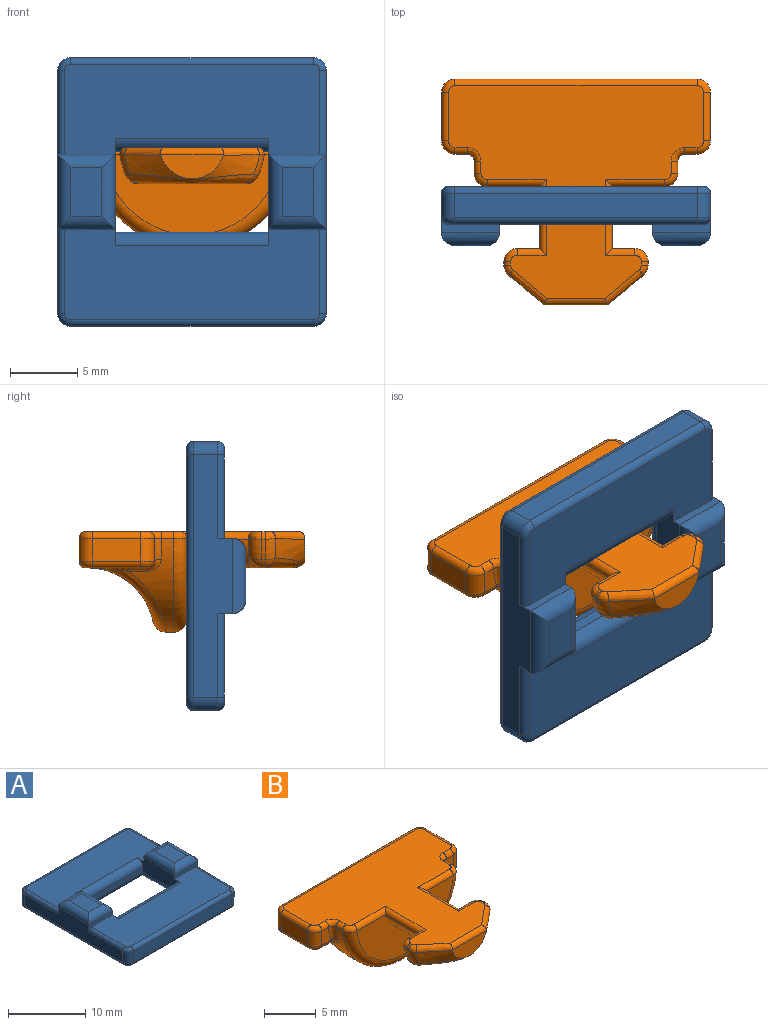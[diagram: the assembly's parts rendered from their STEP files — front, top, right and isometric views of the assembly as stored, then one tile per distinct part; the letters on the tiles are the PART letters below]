
ASSEMBLY  parts=2 mates=1
PART A: 53 faces, bbox 20.2x20.2x4.4 mm
  f0: plane 19x6.7mm, normal (0,0,1), area 113.5mm2, adj f6,f8,f12,f15,f33,f48,f49,f50
  f1: plane 19x6.7mm, normal (0,0,1), area 113.5mm2, adj f6,f8,f11,f14,f34,f43,f44,f45
  f2: plane 18x2.9mm, normal (1,0,0), area 38.6mm2, adj f11,f12,f18,f26,f28,f38,f47,f52
  f3: plane 18x1.8mm, normal (0,1,0), area 32.4mm2, adj f27,f28,f35,f45
  f4: plane 18x2.9mm, normal (-1,0,0), area 38.6mm2, adj f14,f15,f22,f25,f27,f39,f43,f48
  f5: plane 11.4x0.8mm, normal (0,-1,0), area 9.1mm2, adj f6,f8,f30,f34
  f6: plane 8x2.4mm, normal (-1,0,0), area 14.6mm2, adj f0,f1,f5,f7,f11,f12,f19,f29
  f7: plane 11.4x0.8mm, normal (0,1,0), area 9.1mm2, adj f6,f8,f31,f33
  f8: plane 8x2.4mm, normal (1,0,0), area 14.6mm2, adj f0,f1,f5,f7,f14,f15,f23,f32
  f9: plane 18x1.8mm, normal (0,-1,0), area 32.4mm2, adj f25,f26,f42,f50
  f10: plane 19x19mm, normal (0,0,-1), area 253.6mm2, adj f29,f30,f31,f32,f35,f36,f37,f38
  f11: plane 4.3x1.1mm, normal (0,1,0), area 2.6mm2, adj f1,f2,f6,f17,f47
  f12: plane 4.3x1.1mm, normal (0,-1,0), area 2.6mm2, adj f0,f2,f6,f20,f52
  f13: plane 3.6x2.3mm, normal (0,0,1), area 8.3mm2, adj f17,f18,f19,f20
  f14: plane 4.3x1.1mm, normal (0,1,0), area 2.6mm2, adj f1,f4,f8,f24,f43
  f15: plane 4.3x1.1mm, normal (0,-1,0), area 2.6mm2, adj f0,f4,f8,f21,f48
  f16: plane 3.6x2.3mm, normal (0,0,1), area 8.3mm2, adj f21,f22,f23,f24
  f17: cylinder r=1mm len=4.3mm, axis (1,0,0), area 5.6mm2, adj f11,f13,f18,f19
  f18: cylinder r=1mm len=5.6mm, axis (0,-1,0), area 7.7mm2, adj f2,f13,f17,f20
  f19: cylinder r=1mm len=5.6mm, axis (0,1,0), area 7.7mm2, adj f6,f13,f17,f20
  f20: cylinder r=1mm len=4.3mm, axis (-1,0,0), area 5.6mm2, adj f12,f13,f18,f19
  f21: cylinder r=1mm len=4.3mm, axis (-1,0,0), area 5.6mm2, adj f15,f16,f22,f23
  f22: cylinder r=1mm len=5.6mm, axis (0,1,0), area 7.7mm2, adj f4,f16,f21,f24
  f23: cylinder r=1mm len=5.6mm, axis (0,-1,0), area 7.7mm2, adj f8,f16,f21,f24
  f24: cylinder r=1mm len=4.3mm, axis (1,0,0), area 5.6mm2, adj f14,f16,f22,f23
  f25: cylinder r=1mm len=1.8mm, axis (0,0,1), area 2.8mm2, adj f4,f9,f41,f49
  f26: cylinder r=1mm len=1.8mm, axis (0,0,-1), area 2.8mm2, adj f2,f9,f40,f51
  f27: cylinder r=1mm len=1.8mm, axis (0,0,-1), area 2.8mm2, adj f3,f4,f37,f44
  f28: cylinder r=1mm len=1.8mm, axis (0,0,1), area 2.8mm2, adj f2,f3,f36,f46
  f29: cylinder r=1mm len=8mm, axis (0,-1,0), area 10.6mm2, adj f6,f10,f30,f31
  f30: cylinder r=1mm len=13.4mm, axis (1,0,0), area 19mm2, adj f5,f10,f29,f32
  f31: cylinder r=1mm len=13.4mm, axis (-1,0,0), area 19mm2, adj f7,f10,f29,f32
  f32: cylinder r=1mm len=8mm, axis (0,1,0), area 10.6mm2, adj f8,f10,f30,f31
  f33: cylinder r=1mm len=11.4mm, axis (1,0,0), area 17.9mm2, adj f0,f6,f7,f8
  f34: cylinder r=1mm len=11.4mm, axis (-1,0,0), area 17.9mm2, adj f1,f5,f6,f8
  f35: cylinder r=0.5mm len=18mm, axis (-1,0,0), area 14.1mm2, adj f3,f10,f36,f37
  f36: torus R=0.5mm, axis (0,0,1), area 1mm2, adj f10,f28,f35,f38
  f37: torus R=0.5mm, axis (0,0,1), area 1mm2, adj f10,f27,f35,f39
  f38: cylinder r=0.5mm len=18mm, axis (0,1,0), area 14.1mm2, adj f2,f10,f36,f40
  f39: cylinder r=0.5mm len=18mm, axis (0,-1,0), area 14.1mm2, adj f4,f10,f37,f41
  f40: torus R=0.5mm, axis (0,0,1), area 1mm2, adj f10,f26,f38,f42
  f41: torus R=0.5mm, axis (0,0,1), area 1mm2, adj f10,f25,f39,f42
  f42: cylinder r=0.5mm len=18mm, axis (1,0,0), area 14.1mm2, adj f9,f10,f40,f41
  f43: cylinder r=0.5mm len=6.2mm, axis (0,1,0), area 4.9mm2, adj f1,f4,f14,f44
  f44: torus R=0.5mm, axis (0,0,1), area 1mm2, adj f1,f27,f43,f45
  f45: cylinder r=0.5mm len=18mm, axis (1,0,0), area 14.1mm2, adj f1,f3,f44,f46
  f46: torus R=0.5mm, axis (0,0,1), area 1mm2, adj f1,f28,f45,f47
  f47: cylinder r=0.5mm len=6.2mm, axis (0,-1,0), area 4.9mm2, adj f1,f2,f11,f46
  f48: cylinder r=0.5mm len=6.2mm, axis (0,1,0), area 4.9mm2, adj f0,f4,f15,f49
  f49: torus R=0.5mm, axis (0,0,1), area 1mm2, adj f0,f25,f48,f50
  f50: cylinder r=0.5mm len=18mm, axis (-1,0,0), area 14.1mm2, adj f0,f9,f49,f51
  f51: torus R=0.5mm, axis (0,0,1), area 1mm2, adj f0,f26,f50,f52
  f52: cylinder r=0.5mm len=6.2mm, axis (0,-1,0), area 4.9mm2, adj f0,f2,f12,f51
PART B: 86 faces, bbox 40.2x41.7x32.7 mm
  f0: plane 3.6x1.7mm, normal (-1,0,0), area 6.1mm2, adj f1,f83,f84,f85
  f1: cylinder r=0.5mm len=3.6mm, axis (0,1,0), area 2.8mm2, adj f0,f2,f81,f82
  f2: plane 39x24.6mm, normal (0,0,-1), area 22.9mm2, adj f1,f3,f71,f72,f73,f74,f75,f76
  f3: cylinder r=0.5mm len=1.6mm, axis (1,0,0), area 1.1mm2, adj f2,f4,f70,f71
  f4: bspline ~1.21x1.06mm, area 0.8mm2, adj f3,f5,f68,f80
  f5: torus R=8.1mm, axis (0,-1,0), area 1.3mm2, adj f4,f6,f68,f70
  f6: bspline ~1.23x1.06mm, area 0.9mm2, adj f5,f7,f66,f67
  f7: plane 19x15.8mm, normal (0,0,1), area 171.3mm2, adj f6,f8,f12,f13,f14,f15,f20,f21
  f8: bspline ~1.23x1.22mm, area 0.9mm2, adj f7,f9,f12,f65
  f9: torus R=8.1mm, axis (0,-1,0), area 1.3mm2, adj f8,f10,f11,f68
  f10: plane 1.72x1.23mm, normal (0,-1,0), area 1.8mm2, adj f9,f12,f75,f85
  f11: bspline ~1.15x1.06mm, area 0.8mm2, adj f9,f68,f75,f76
  f12: cylinder r=0.5mm len=0.92mm, axis (-1,0,0), area 0.7mm2, adj f7,f8,f10,f13
  f13: torus R=0.5mm, axis (0,0,1), area 1mm2, adj f7,f12,f84,f85
  f14: torus R=0.5mm, axis (0,0,1), area 1mm2, adj f7,f15,f83,f84
  f15: cylinder r=0.5mm len=18mm, axis (1,0,0), area 14.1mm2, adj f7,f14,f16,f20
  f16: plane 18x1.7mm, normal (0,1,0), area 30.6mm2, adj f15,f17,f74,f83
  f17: cylinder r=1mm len=1.7mm, axis (0,0,1), area 2.7mm2, adj f16,f18,f20,f73
  f18: plane 3.6x1.7mm, normal (1,0,0), area 6.1mm2, adj f17,f19,f21,f72
  f19: cylinder r=1mm len=1.7mm, axis (0,0,-1), area 2.7mm2, adj f18,f22,f70,f71
  f20: torus R=0.5mm, axis (0,0,1), area 1mm2, adj f7,f15,f17,f21
  f21: cylinder r=0.5mm len=3.6mm, axis (0,-1,0), area 2.8mm2, adj f7,f18,f20,f22
  f22: torus R=0.5mm, axis (0,0,1), area 1mm2, adj f7,f19,f21,f66
  f23: bspline ~1.23x1.1mm, area 1.1mm2, adj f7,f24,f49,f67
  f24: torus R=6.6mm, axis (0,1,0), area 33.7mm2, adj f23,f25,f64,f68
  f25: plane 13.2x6.05mm, normal (0,-1,0), area 51.5mm2, adj f24,f26,f49,f50,f62,f63
  f26: cylinder r=2.8mm len=5.41mm, axis (0,1,0), area 33.7mm2, adj f25,f27,f46,f47,f48,f50,f62
  f27: plane 2.24x1.22mm, normal (0,1,0), area 2.1mm2, adj f26,f28,f45,f61,f62
  f28: cylinder r=1mm len=1.87mm, axis (1,0,0), area 2.9mm2, adj f27,f29,f44,f46
  f29: sphere r=1mm, area 1.2mm2, adj f28,f30,f45
  f30: cylinder r=1mm len=0.91mm, axis (0,1,0), area 0.3mm2, adj f29,f31,f43,f44
  f31: cylinder r=5.4mm len=1.55mm, axis (0,1,0), area 0.4mm2, adj f30,f32,f45,f59
  f32: torus R=4.4mm, axis (0,1,0), area 1.4mm2, adj f31,f33,f43,f58
  f33: cone r=5.4mm half-angle=50deg, axis (0,1,0), area 11.6mm2, adj f32,f34,f41,f42,f55,f57
  f34: bspline ~10.74x3.6mm, area 10.9mm2, adj f33,f35,f43,f44
  f35: sphere r=1mm, area 0.6mm2, adj f34,f36,f42
  f36: cylinder r=1mm len=0.91mm, axis (0,1,0), area 0.3mm2, adj f35,f37,f39,f44
  f37: cylinder r=5.4mm len=1.55mm, axis (0,1,0), area 0.4mm2, adj f36,f38,f42,f53
  f38: torus R=4.4mm, axis (0,-1,0), area 2.3mm2, adj f37,f39,f48,f52
  f39: sphere r=1mm, area 1.2mm2, adj f36,f38,f40
  f40: cylinder r=1mm len=1.87mm, axis (1,0,0), area 2.9mm2, adj f39,f44,f47,f48
  f41: plane 4.67x1.83mm, normal (0,-1,0), area 6.3mm2, adj f33,f55,f56,f57
  f42: torus R=4.4mm, axis (0,-1,0), area 1.4mm2, adj f33,f35,f37,f54
  f43: sphere r=1mm, area 0.6mm2, adj f30,f32,f34
  f44: plane 8.03x3.42mm, normal (0,0,-1), area 14.1mm2, adj f28,f30,f34,f36,f40,f46,f47
  f45: torus R=4.4mm, axis (0,-1,0), area 2.3mm2, adj f27,f29,f31,f60
  f46: bspline ~2.44x1.15mm, area 1.1mm2, adj f26,f28,f44
  f47: bspline ~2.44x1.15mm, area 1.1mm2, adj f26,f40,f44
  f48: plane 2.24x1.22mm, normal (0,1,0), area 2.1mm2, adj f26,f38,f40,f50,f51
  f49: cylinder r=0.5mm len=4.35mm, axis (-1,0,0), area 3.2mm2, adj f7,f23,f25,f50
  f50: cylinder r=0.5mm len=5.6mm, axis (0,1,0), area 4.5mm2, adj f7,f25,f26,f48,f49,f51
  f51: cylinder r=0.5mm len=2.14mm, axis (1,0,0), area 1.5mm2, adj f7,f48,f50,f52
  f52: bspline ~1.24x1.13mm, area 1.1mm2, adj f7,f38,f51,f53
  f53: cylinder r=0.5mm len=0.56mm, axis (0,1,0), area 0.2mm2, adj f7,f37,f52,f54
  f54: bspline ~1.07x0.77mm, area 0.6mm2, adj f7,f42,f53,f55
  f55: bspline ~4.22x3.68mm, area 2.9mm2, adj f7,f33,f41,f54,f56
  f56: cylinder r=0.5mm len=4.67mm, axis (-1,0,0), area 3.5mm2, adj f7,f41,f55,f57
  f57: bspline ~4.22x3.68mm, area 2.9mm2, adj f7,f33,f41,f56,f58
  f58: bspline ~0.98x0.84mm, area 0.6mm2, adj f7,f32,f57,f59
  f59: cylinder r=0.5mm len=0.56mm, axis (0,1,0), area 0.2mm2, adj f7,f31,f58,f60
  f60: bspline ~1.24x1.13mm, area 1.1mm2, adj f7,f45,f59,f61
  f61: cylinder r=0.5mm len=2.14mm, axis (1,0,0), area 1.5mm2, adj f7,f27,f60,f62
  f62: cylinder r=0.5mm len=5.6mm, axis (0,1,0), area 4.5mm2, adj f7,f25,f26,f27,f61,f63
  f63: cylinder r=0.5mm len=4.35mm, axis (-1,0,0), area 3.2mm2, adj f7,f25,f62,f64
  f64: bspline ~1.27x1.23mm, area 1.1mm2, adj f7,f24,f63,f65
  f65: cylinder r=0.5mm len=0.9mm, axis (0,1,0), area 0.7mm2, adj f7,f8,f64,f68
  f66: cylinder r=0.5mm len=0.92mm, axis (-1,0,0), area 0.7mm2, adj f6,f7,f22,f70
  f67: cylinder r=0.5mm len=0.9mm, axis (0,1,0), area 0.7mm2, adj f6,f7,f23,f68
  f68: cylinder r=7.6mm len=15.15mm, axis (0,1,0), area 25.8mm2, adj f4,f5,f9,f11,f24,f65,f67,f69
  f69: bspline ~14.63x6.87mm, area 25.6mm2, adj f68,f77,f78,f79
  f70: plane 1.72x1.23mm, normal (0,-1,0), area 1.8mm2, adj f3,f5,f19,f66
  f71: torus R=0.5mm, axis (0,0,1), area 1mm2, adj f2,f3,f19,f72
  f72: cylinder r=0.5mm len=3.6mm, axis (0,1,0), area 2.8mm2, adj f2,f18,f71,f73
  f73: torus R=0.5mm, axis (0,0,1), area 1mm2, adj f2,f17,f72,f74
  f74: cylinder r=0.5mm len=18mm, axis (-1,0,0), area 14.1mm2, adj f2,f16,f73,f81
  f75: cylinder r=0.5mm len=1.6mm, axis (1,0,0), area 1.1mm2, adj f2,f10,f11,f82
  f76: cylinder r=0.5mm len=1.36mm, axis (0,1,0), area 0.8mm2, adj f2,f11,f68,f77
  f77: bspline ~3.14x1.05mm, area 0.6mm2, adj f2,f69,f76
  f78: cylinder r=5mm len=12.7mm, axis (1,0,0), area 0mm2, adj f2,f69
  f79: bspline ~3.94x1.05mm, area 0.6mm2, adj f2,f69,f80
  f80: cylinder r=0.5mm len=1.36mm, axis (0,1,0), area 0.8mm2, adj f2,f4,f68,f79
  f81: torus R=0.5mm, axis (0,0,1), area 1mm2, adj f1,f2,f74,f83
  f82: torus R=0.5mm, axis (0,0,1), area 1mm2, adj f1,f2,f75,f85
  f83: cylinder r=1mm len=1.7mm, axis (0,0,1), area 2.7mm2, adj f0,f14,f16,f81
  f84: cylinder r=0.5mm len=3.6mm, axis (0,1,0), area 2.8mm2, adj f0,f7,f13,f14
  f85: cylinder r=1mm len=1.7mm, axis (0,0,-1), area 2.7mm2, adj f0,f10,f13,f82
PLACE A rot(axis=(1,0,0),90deg) t=(-28,-1.37,-6.78)mm
PLACE B t=(0,-0.49,-3.37)mm
MATE fastened A.f10 <-> B.f25  axis (0,1,0) through (0,0.03,-6.78)mm
